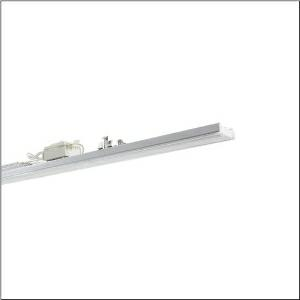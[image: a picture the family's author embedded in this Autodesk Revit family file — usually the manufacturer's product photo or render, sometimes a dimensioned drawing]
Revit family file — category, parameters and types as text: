
# Revit family: licross_r__11_recessed_ho_51tl12dn4exm_ac63
name_source: partatom
category: Lighting Fixtures
units: mm (PartAtom-declared; Revit-internal decimal feet)

## family parameters
Cut with Voids When Loaded = No
Host = Face
Light Source = No
Part Type = Normal
Room Calculation Point = No
Round Connector Dimension = Use Diameter
Shared = No

## types (1)
- --- (1 x LED, 14030 lm, 76.8 W, 4000K)
    Apparent Load = 77 VA
    CIE Flux Codes = 66 91 98 100 100
    Color Rendering = 80
    Color Temperature = 4000K
    Default Elevation = 1800 mm
    Description = Licross® 11 Recessed HO, luminaire insert, of sheet steel, coil coated, white, length: 1.500mm, width: 66mm, height: 67mm, LED rated luminous flux: 14.030lm, light colour: 840, control gear: DALI 2, with plug, 5-pole, with phase selection, mains connection: 220..240V, AC, 50/60Hz, rated input power: 77W, halogen-free wiring, primary optical cover: cover, of PMMA, light emission: direct distribution, primary light characteristic: symmetric, protection rating (complete): IP40, insulation class (complete): insulation class I (protective earthing), certification: CE, ENEC, VDE, UKCA, protection symbol: D if used in an environment without relevant dust loads with corresponding accessories, impact resistance: IK06, permissible ambient temperature for indoor applications: -25..+30°C, corresponds to IFS (International Featured Standards) requirements for safety and quality in the food industry, reducing of maximum allowable ambient temperature of 5°C with ceiling mounting, LABS conformity tested according to VDMA 24364:2018-05, packaging unit: 1 piece
    Height = 58 mm
    Lamp = 1 x LED
    Lamp Light Flux = 14030 lm
    Lamp Power = 76.8 W
    Lamp count = 1
    Length = 1500 mm
    Luminous efficacy = 183 lm/W
    Manufacturer = Siteco
    ModVariant = No
    Model = 51TL12DN4EXM
    Mounting Place = Ceiling
    Mounting Type = Pendant
    Number of Poles = 1
    OnlyDefault = Yes
    Power Factor = 1
    Product Name = Licross® 11 Recessed HO
    Product group = luminaire insert
    ProductGroupID = 902
    Protection Class = Protection class I
    Protection Degree = IP 40
    RLX_Detail_Level = 1
    RLX_Emergency_Light_Flux = 0 lm
    RLX_Emergency_Type = 0
    RLX_Emergency_Type_DB = No
    RlxData = <blob elided: 24601 chars, md5=31b2734f>
    Socket = socket
    Standby Power = 0 W
    System Light Flux = 14030 lm
    System Power = 77 W
    Type Comments = factory setting: luminous flux: 100 % | dim-lin: 254 | 522 mA
    Type Image = l_1296930.jpg
    URL = http://relux.com
    VarID = @adj_010725
    Voltage = 0 V
    Weight = 0.00 kg
    Width = 66 mm

## geometry (parser evidence)
native form markers: Blend x4, Sweep x11
no freeform markers — native parametric forms only
